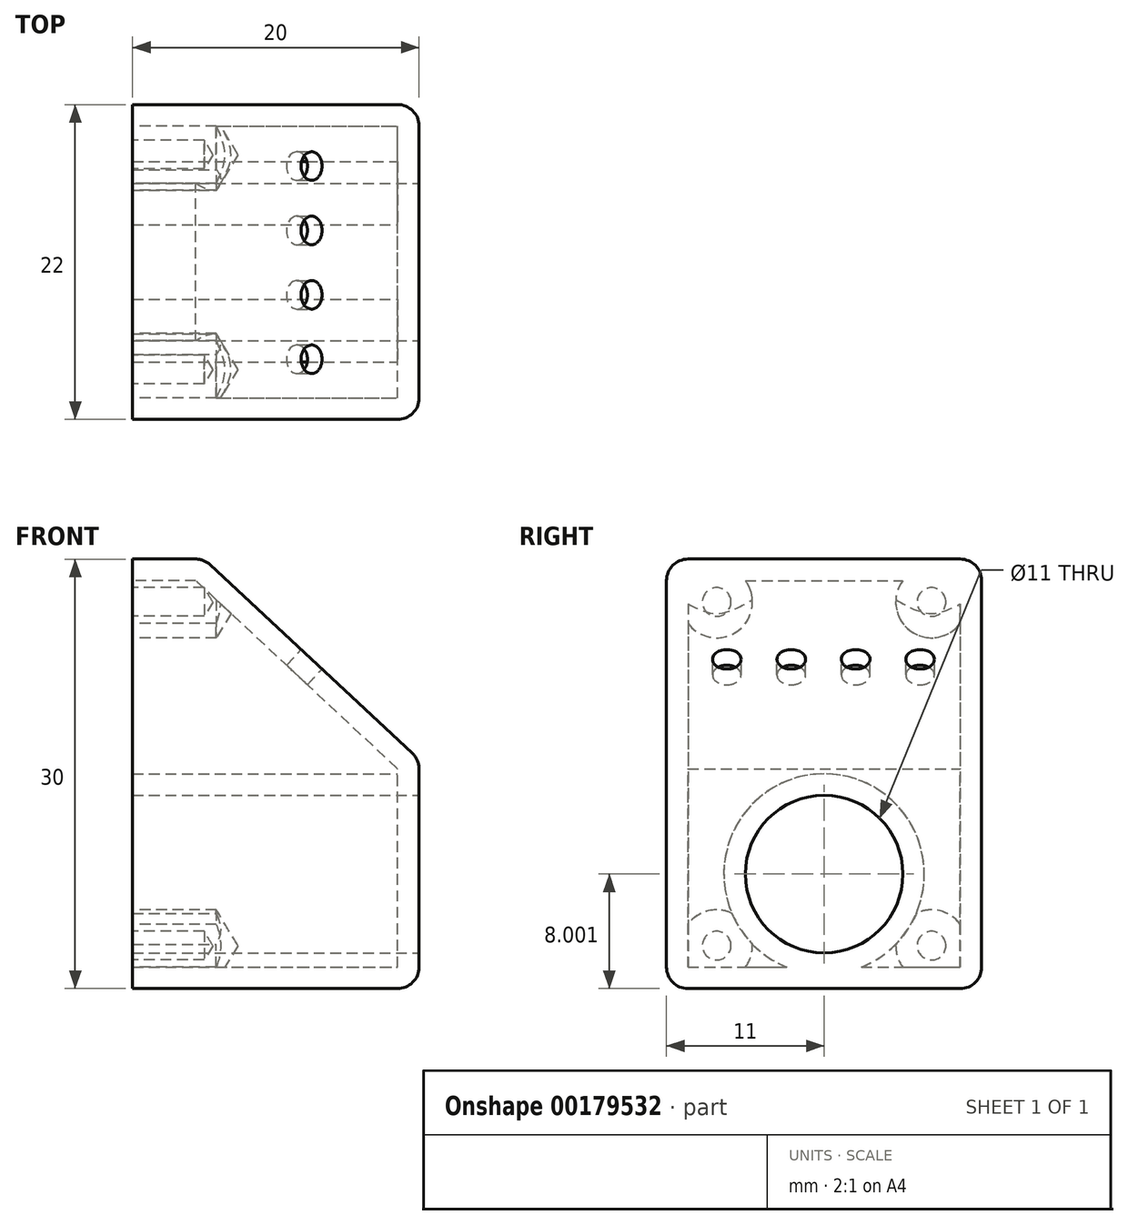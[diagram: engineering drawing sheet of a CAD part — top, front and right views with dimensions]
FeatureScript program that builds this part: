
annotation { "Feature Type Name" : "Feature", "Feature Type Description" : "" }
export const myFeature = defineFeature(function(context is Context, id is Id, definition is map)
    precondition{}
    {
        {
            var Q0;
            Q0=qCreatedBy(makeId("Front.planeOp"),FACE);
            var sketch = newSketch(context, id + "F0", { "sketchPlane" : qUnion([Q0])});
            skLineSegment(sketch, "E0", {"start": v(-22.65, 12.5) * mm, "end": v(-2.65, 12.5) * mm});
            skLineSegment(sketch, "E1", {"start": v(-2.65, 12.5) * mm, "end": v(-2.65, 28.5) * mm});
            skLineSegment(sketch, "E2", {"start": v(-22.65, 42.5) * mm, "end": v(-22.65, 12.5) * mm});
            skLineSegment(sketch, "E3", {"start": v(-22.65, 42.5) * mm, "end": v(-17.65, 42.5) * mm});
            skLineSegment(sketch, "E4", {"start": v(-17.65, 42.5) * mm, "end": v(-2.65, 28.5) * mm});
            skSolve(sketch);
        }
        {
            var Q0;
            Q0 = qSketchRegion(id + "F0", true);
            extrude(context, id + "F1", {"entities" : qUnion([Q0]), "depth" : 22 * mm});
        }
        {
            var Q0;
            Q0=makeQuery(id+"F1.opExtrude","SWEPT_FACE",FACE,{"disambiguationData":[OSD([sQuery(id+"F0.wireOp",EDGE,"E1")])]});
            var sketch = newSketch(context, id + "F2", { "sketchPlane" : qUnion([Q0])});
            skPoint(sketch, "E5", {"position": v(-11, 20.5) * mm});
            skPoint(sketch, "E5.positionSnap0", {"position": v(-22, 20.5) * mm});
            skPoint(sketch, "E5.positionSnap1", {"position": v(-11, 12.5) * mm});
            skSolve(sketch);
        }
        {
            var Q0;
            Q0=sQuery(id+"F2.wireOp",VERTEX,"E5");
            var Q1;
            Q1=makeQuery(id+"F1.opExtrude","SWEPT_BODY",BODY,{"disambiguationData":[OSD([sQuery(id+"F0.wireOp",EDGE,"E0"),sQuery(id+"F0.wireOp",EDGE,"E1"),sQuery(id+"F0.wireOp",EDGE,"PUZHJhJu-nJOz-g8jR-lthh-dLy8XL8XWcud"),sQuery(id+"F0.wireOp",EDGE,"E2")])]});
            hole(context, id + "F3", {"style" : HoleStyle.SIMPLE, "endStyle" : HoleEndStyle.THROUGH, "holeDiameter" : 11 * mm, "startFromSketch" : true, "locations" : qUnion([Q0]), "scope" : qUnion([Q1]), "isTappedThrough" : true});
        }
        {
            var Q0;
            Q0=makeQuery(id+"F1.opExtrude","SWEPT_FACE",FACE,{"disambiguationData":[OSD([sQuery(id+"F0.wireOp",EDGE,"E2")])]});
            var sketch = newSketch(context, id + "F4", { "sketchPlane" : qUnion([Q0])});
            skPoint(sketch, "E6", {"position": v(3.5, 15.5) * mm});
            skPoint(sketch, "E7", {"position": v(18.5, 15.5) * mm});
            skPoint(sketch, "E8", {"position": v(3.5, 39.5) * mm});
            skPoint(sketch, "E9", {"position": v(18.5, 39.5) * mm});
            skSolve(sketch);
        }
        {
            var Q0;
            Q0=sQuery(id+"F4.wireOp",VERTEX,"E6");
            var Q1;
            Q1=sQuery(id+"F4.wireOp",VERTEX,"E7");
            var Q2;
            Q2=sQuery(id+"F4.wireOp",VERTEX,"E8");
            var Q3;
            Q3=sQuery(id+"F4.wireOp",VERTEX,"E9");
            var Q4;
            Q4=makeQuery(id+"F1.opExtrude","SWEPT_BODY",BODY,{"disambiguationData":[OSD([sQuery(id+"F0.wireOp",EDGE,"E0"),sQuery(id+"F0.wireOp",EDGE,"E1"),sQuery(id+"F0.wireOp",EDGE,"PUZHJhJu-nJOz-g8jR-lthh-dLy8XL8XWcud"),sQuery(id+"F0.wireOp",EDGE,"E2")])]});
            hole(context, id + "F5", {"style" : HoleStyle.SIMPLE, "endStyle" : HoleEndStyle.BLIND, "holeDiameter" : 2 * mm, "holeDepth" : 5 * mm, "startFromSketch" : true, "locations" : qUnion([Q0, Q1, Q2, Q3]), "scope" : qUnion([Q4])});
        }
        {
            var Q0;
            Q0=makeQuery(id+"F1.opExtrude","SWEPT_FACE",FACE,{"disambiguationData":[OSD([sQuery(id+"F0.wireOp",EDGE,"E4")])]});
            var sketch = newSketch(context, id + "F6", { "sketchPlane" : qUnion([Q0])});
            skPoint(sketch, "E10", {"position": v(-31.64, -17.8) * mm});
            skPoint(sketch, "E11", {"position": v(-31.64, -13.3) * mm});
            skPoint(sketch, "E12", {"position": v(-31.64, -8.8) * mm});
            skPoint(sketch, "E13", {"position": v(-31.64, -4.3) * mm});
            skLineSegment(sketch, "E14.bottom", {"start": v(-41.9, -22) * mm, "end": v(-21.38, -22) * mm});
            skLineSegment(sketch, "E14.top", {"start": v(-41.9, 0) * mm, "end": v(-21.38, 0) * mm});
            skLineSegment(sketch, "E14.left", {"start": v(-41.9, -22) * mm, "end": v(-41.9, 0) * mm});
            skLineSegment(sketch, "E14.right", {"start": v(-21.38, -22) * mm, "end": v(-21.38, 0) * mm});
            skPoint(sketch, "E15", {"position": v(-31.64, 0) * mm});
            skPoint(sketch, "E16", {"position": v(-31.64, -22) * mm});
            skSolve(sketch);
        }
        {
            var Q0;
            Q0=makeQuery(id+"F3.hole-0.boolean.opBoolean","COPY",FACE,{"derivedFrom":makeQuery(id+"F3.hole-0.opRevolve","SWEPT_FACE",FACE,{"disambiguationData":[OSD([sQuery(id+"F3.hole-0.sketch.wireOp",EDGE,"core_line_2")])]})});
            var Q1;
            Q1=makeQuery(id+"F1.opExtrude","SWEPT_FACE",FACE,{"disambiguationData":[OSD([sQuery(id+"F0.wireOp",EDGE,"E2")])]});
            shell(context, id + "F7", {"entities" : qUnion([Q0, Q1]), "thickness" : 1.5 * mm});
        }
        {
            var Q0;
            Q0=sQuery(id+"F6.wireOp",VERTEX,"E12");
            var Q1;
            Q1=sQuery(id+"F6.wireOp",VERTEX,"E13");
            var Q2;
            Q2=sQuery(id+"F6.wireOp",VERTEX,"E11");
            var Q3;
            Q3=sQuery(id+"F6.wireOp",VERTEX,"E10");
            var Q4;
            Q4=makeQuery(id+"F1.opExtrude","SWEPT_BODY",BODY,{"disambiguationData":[OSD([sQuery(id+"F0.wireOp",EDGE,"E0"),sQuery(id+"F0.wireOp",EDGE,"E1"),sQuery(id+"F0.wireOp",EDGE,"PUZHJhJu-nJOz-g8jR-lthh-dLy8XL8XWcud"),sQuery(id+"F0.wireOp",EDGE,"E2")])]});
            hole(context, id + "F8", {"style" : HoleStyle.SIMPLE, "endStyle" : HoleEndStyle.BLIND, "holeDiameter" : 2 * mm, "holeDepth" : 8 * mm, "startFromSketch" : true, "locations" : qUnion([Q0, Q1, Q2, Q3]), "scope" : qUnion([Q4])});
        }
        {
            var Q0;
            Q0=makeQuery(id+"F1.opExtrude","CAP_EDGE",EDGE,{"disambiguationData":[OSD([sQuery(id+"F0.wireOp",EDGE,"E4")])],"isStart":false});
            var Q1;
            Q1=makeQuery(id+"F1.opExtrude","SWEPT_EDGE",EDGE,{"disambiguationData":[OSD([sQuery(id+"F0.wireOp",EDGE,"E3"),sQuery(id+"F0.wireOp",EDGE,"E4")])]});
            var Q2;
            Q2=makeQuery(id+"F1.opExtrude","CAP_EDGE",EDGE,{"disambiguationData":[OSD([sQuery(id+"F0.wireOp",EDGE,"E3")])],"isStart":false});
            var Q3;
            Q3=makeQuery(id+"F1.opExtrude","SWEPT_EDGE",EDGE,{"disambiguationData":[OSD([sQuery(id+"F0.wireOp",EDGE,"E1"),sQuery(id+"F0.wireOp",EDGE,"E4")])]});
            var Q4;
            Q4=makeQuery(id+"F1.opExtrude","CAP_EDGE",EDGE,{"disambiguationData":[OSD([sQuery(id+"F0.wireOp",EDGE,"E1")])],"isStart":false});
            var Q5;
            Q5=makeQuery(id+"F1.opExtrude","CAP_EDGE",EDGE,{"disambiguationData":[OSD([sQuery(id+"F0.wireOp",EDGE,"E0")])],"isStart":false});
            var Q6;
            Q6=makeQuery(id+"F1.opExtrude","SWEPT_EDGE",EDGE,{"disambiguationData":[OSD([sQuery(id+"F0.wireOp",EDGE,"E0"),sQuery(id+"F0.wireOp",EDGE,"E1")])]});
            var Q7;
            Q7=makeQuery(id+"F1.opExtrude","CAP_EDGE",EDGE,{"disambiguationData":[OSD([sQuery(id+"F0.wireOp",EDGE,"E1")])],"isStart":true});
            var Q8;
            Q8=makeQuery(id+"F1.opExtrude","CAP_EDGE",EDGE,{"disambiguationData":[OSD([sQuery(id+"F0.wireOp",EDGE,"E4")])],"isStart":true});
            var Q9;
            Q9=makeQuery(id+"F1.opExtrude","CAP_EDGE",EDGE,{"disambiguationData":[OSD([sQuery(id+"F0.wireOp",EDGE,"E3")])],"isStart":true});
            var Q10;
            Q10=makeQuery(id+"F1.opExtrude","CAP_EDGE",EDGE,{"disambiguationData":[OSD([sQuery(id+"F0.wireOp",EDGE,"E0")])],"isStart":true});
            fillet(context, id + "F9", {"entities" : qUnion([Q0, Q1, Q2, Q3, Q4, Q5, Q6, Q7, Q8, Q9, Q10]), "radius" : 1.5 * mm, "tangentPropagation" : true, "allowEdgeOverflow" : false});
        }
    });
